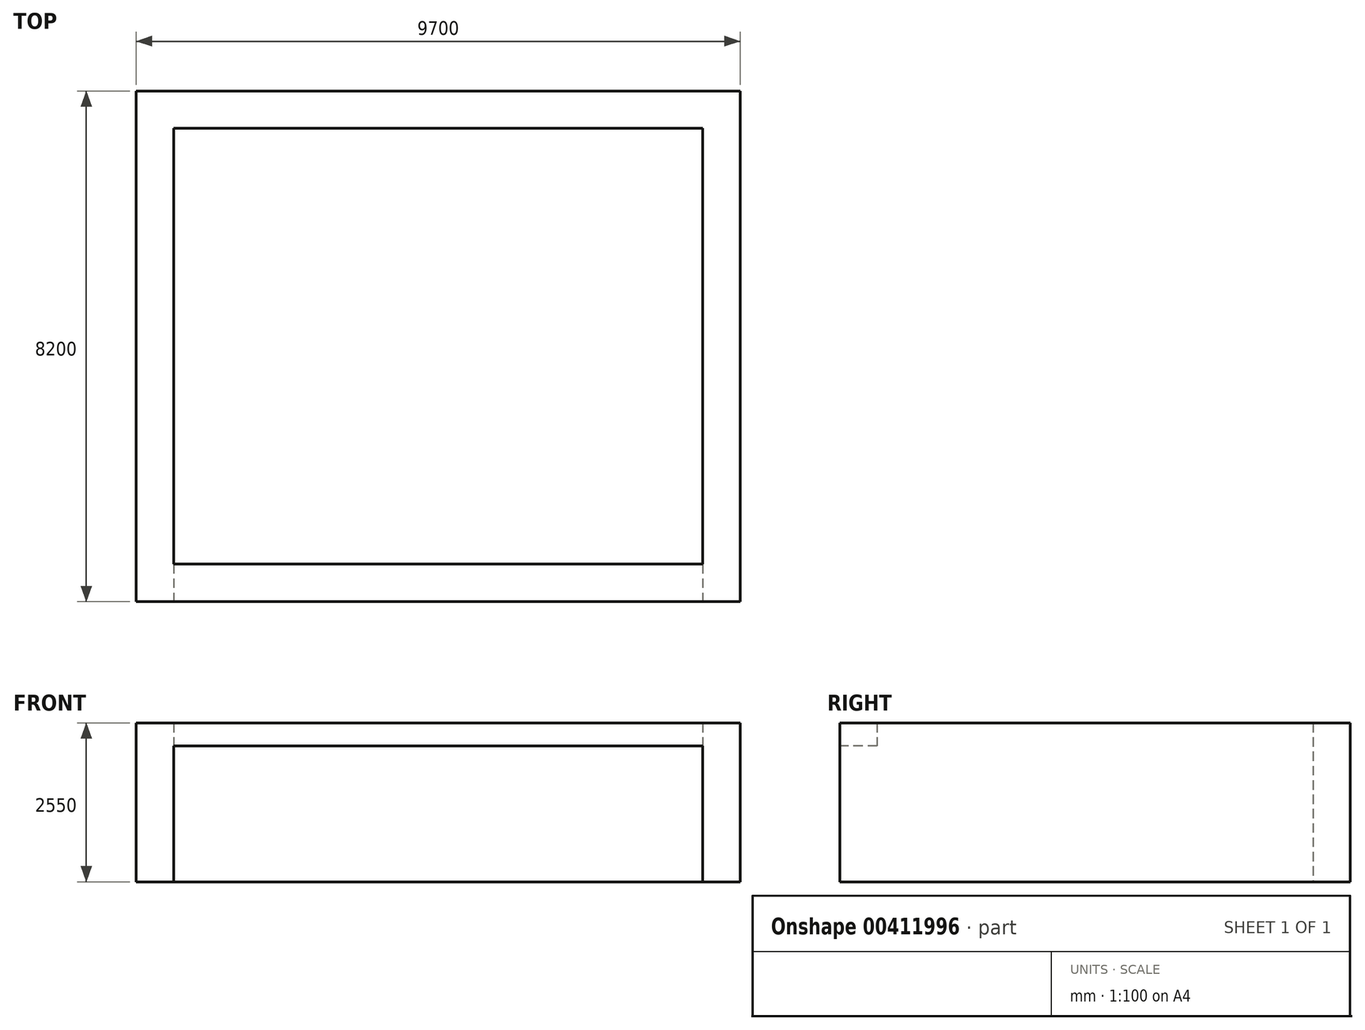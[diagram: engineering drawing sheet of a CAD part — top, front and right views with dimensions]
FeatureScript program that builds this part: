
annotation { "Feature Type Name" : "Feature", "Feature Type Description" : "" }
export const myFeature = defineFeature(function(context is Context, id is Id, definition is map)
    precondition{}
    {
        {
            var Q0;
            Q0=qCreatedBy(makeId("Top.planeOp"),FACE);
            var sketch = newSketch(context, id + "F0", { "sketchPlane" : qUnion([Q0])});
            skLineSegment(sketch, "E0.bottom", {"start": v(8500, 7000) * mm, "end": v(0, 7000) * mm});
            skLineSegment(sketch, "E0.top", {"start": v(8500, 0) * mm, "end": v(0, 0) * mm});
            skLineSegment(sketch, "E0.left", {"start": v(8500, 7000) * mm, "end": v(8500, 0) * mm});
            skLineSegment(sketch, "E0.right", {"start": v(0, 7000) * mm, "end": v(0, 0) * mm});
            skLineSegment(sketch, "E1.bottom", {"start": v(-600, 7600) * mm, "end": v(9100, 7600) * mm});
            skLineSegment(sketch, "E1.top", {"start": v(-600, -600) * mm, "end": v(9100, -600) * mm});
            skLineSegment(sketch, "E1.left", {"start": v(-600, 7600) * mm, "end": v(-600, -600) * mm});
            skLineSegment(sketch, "E1.right", {"start": v(9100, 7600) * mm, "end": v(9100, -600) * mm});
            skSolve(sketch);
        }
        {
            var Q0;
            Q0 = qSketchRegion(id + "F0", true);
            extrude(context, id + "F1", {"entities" : qUnion([Q0]), "depth" : 2550 * mm});
        }
        {
            var Q0;
            Q0=makeQuery(id+"F1.opExtrude","SWEPT_FACE",FACE,{"disambiguationData":[OSD([sQuery(id+"F0.wireOp",EDGE,"E1.top")])]});
            var sketch = newSketch(context, id + "F2", { "sketchPlane" : qUnion([Q0])});
            skLineSegment(sketch, "E2.bottom", {"start": v(0, 0) * mm, "end": v(8500, 0) * mm});
            skLineSegment(sketch, "E2.top", {"start": v(0, 2180) * mm, "end": v(8500, 2180) * mm});
            skLineSegment(sketch, "E2.left", {"start": v(0, 0) * mm, "end": v(0, 2180) * mm});
            skLineSegment(sketch, "E2.right", {"start": v(8500, 0) * mm, "end": v(8500, 2180) * mm});
            skSolve(sketch);
        }
        {
            var Q0;
            Q0 = qSketchRegion(id + "F2", true);
            var Q1;
            Q1=makeQuery(id+"F1.opExtrude","SWEPT_FACE",FACE,{"disambiguationData":[OSD([sQuery(id+"F0.wireOp",EDGE,"E0.top")])]});
            extrude(context, id + "F3", {"entities" : qUnion([Q0]), "operationType" : NewBodyOperationType.REMOVE, "oppositeDirection" : true, "endBoundEntityFace" : qUnion([Q1]), "depth" : 1000 * mm});
        }
    });
